# Revit family: BS 50 Urinal
name_source: partatom
category: Plumbing Fixtures
units: mm (PartAtom-declared; Revit-internal decimal feet)

## family parameters
Always vertical = Yes
Cut with Voids When Loaded = No
Enable Cutting in Views = No
Maintain Annotation Orientation = No
OmniClass Number = 23.45.05.21.11.21
OmniClass Title = Urinals
Part Type = Normal
Room Calculation Point = No
Round Connector Dimension = Use Diameter
Shared = No
Work Plane-Based = No

## types (2) — shared parameters
Category = Urinals
Colour = White
Description = Includes 2 x brackets & waste
Manufacturer = Lecico SA
Material = Vitreous China
Technical Dimensions = W380 x H500 x D302mm
URL = https://www.lecicosa.co.za
zero-valued in all types: Default Elevation

## per-type parameters (varying)
| type | Product Code |
| BS 50 Urinal (TE spreader) | ATLBOXURI0T50UE |
| BS 50 Urinal (BE spreader) | ATLBOXURI0B50UE |

note: column(s) folded — value = type name in every type: Model

## geometry (parser evidence)
native form markers: Sweep x3
no freeform markers — native parametric forms only
